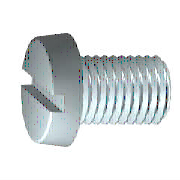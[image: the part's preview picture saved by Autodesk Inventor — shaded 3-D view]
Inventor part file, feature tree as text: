
AUTODESK INVENTOR PART (.ipt)
format: ipt  version: 2024.2 (Build 282272000, 272)  size: 188,928 bytes
history: native  units: mm (DEFAULTED — no unit token found)
features: extrude x1, plane x1
ambient origin geometry x7: Origin, YZ Plane, XZ Plane, X Axis, Y Axis, Z Axis, Center Point
bodies: Solid1 (feature_tree), Body (feature_tree)
feature tree (2):
  extrude  "Slot"  Depth=16.0mm
  plane  "Work Plane1"
